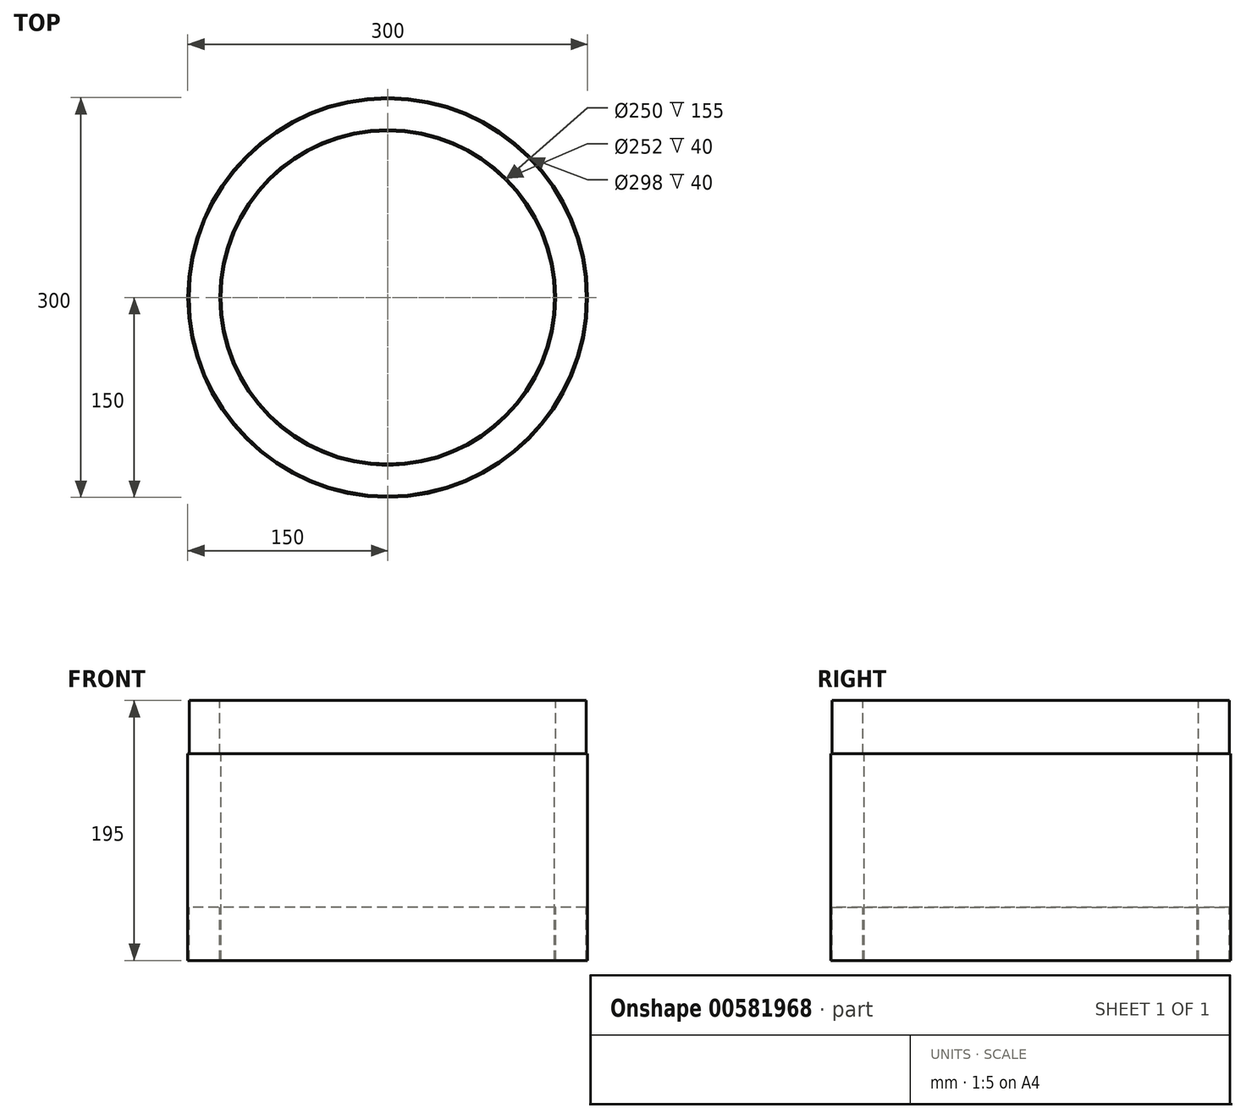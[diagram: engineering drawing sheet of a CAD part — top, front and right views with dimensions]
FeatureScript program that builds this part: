
annotation { "Feature Type Name" : "Feature", "Feature Type Description" : "" }
export const myFeature = defineFeature(function(context is Context, id is Id, definition is map)
    precondition{}
    {
        {
            var Q0;
            Q0=qCreatedBy(makeId("Front.planeOp"),FACE);
            var sketch = newSketch(context, id + "F0", { "sketchPlane" : qUnion([Q0])});
            skLineSegment(sketch, "E0", {"start": v(0, 345.75) * mm, "end": v(0, -558.03) * mm, "construction": true});
            skLineSegment(sketch, "E1", {"start": v(-125, -518.84) * mm, "end": v(-125, -363.84) * mm});
            skLineSegment(sketch, "E2", {"start": v(-125, -363.84) * mm, "end": v(-126, -363.84) * mm});
            skLineSegment(sketch, "E3", {"start": v(-126, -363.84) * mm, "end": v(-126, -323.84) * mm});
            skLineSegment(sketch, "E4", {"start": v(-126, -323.84) * mm, "end": v(-149, -323.84) * mm});
            skLineSegment(sketch, "E5", {"start": v(-149, -323.84) * mm, "end": v(-149, -363.84) * mm});
            skLineSegment(sketch, "E6", {"start": v(-149, -363.84) * mm, "end": v(-150, -363.84) * mm});
            skLineSegment(sketch, "E7", {"start": v(-150, -363.84) * mm, "end": v(-150, -518.84) * mm});
            skLineSegment(sketch, "E8", {"start": v(-150, -518.84) * mm, "end": v(-149, -518.84) * mm});
            skLineSegment(sketch, "E9", {"start": v(-149, -518.84) * mm, "end": v(-149, -478.84) * mm});
            skLineSegment(sketch, "E10", {"start": v(-149, -478.84) * mm, "end": v(-126, -478.84) * mm});
            skLineSegment(sketch, "E11", {"start": v(-126, -478.84) * mm, "end": v(-126, -518.84) * mm});
            skLineSegment(sketch, "E12", {"start": v(-126, -518.84) * mm, "end": v(-125, -518.84) * mm});
            skSolve(sketch);
        }
        {
            var Q0;
            Q0=qSketchRegion(id+"F0",true);
            var Q1;
            Q1=sQuery(id+"F0.wireOp",EDGE,"E0");
            revolve(context, id + "F1", {"entities" : qUnion([Q0]), "axis" : qUnion([Q1]), "revolveType" : RevolveType.FULL});
        }
    });
